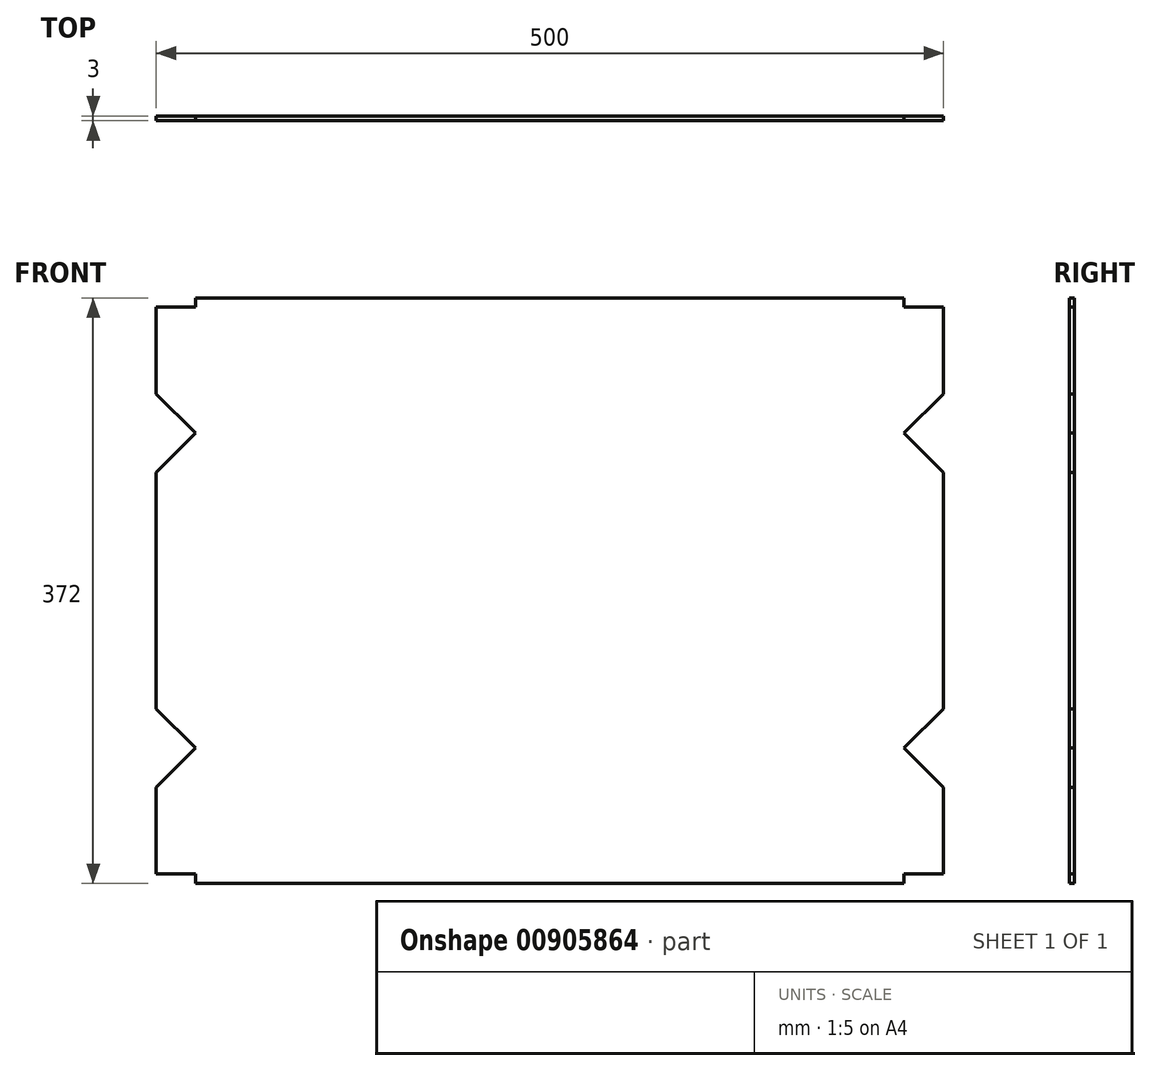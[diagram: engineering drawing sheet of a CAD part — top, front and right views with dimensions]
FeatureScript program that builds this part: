
annotation { "Feature Type Name" : "Feature", "Feature Type Description" : "" }
export const myFeature = defineFeature(function(context is Context, id is Id, definition is map)
    precondition{}
    {
        {
            var Q0;
            Q0=qCreatedBy(makeId("Front.planeOp"),FACE);
            var sketch = newSketch(context, id + "F0", { "sketchPlane" : qUnion([Q0])});
            skLineSegment(sketch, "E0.bottom", {"start": v(225, 186) * mm, "end": v(-225, 186) * mm});
            skLineSegment(sketch, "E0.top", {"start": v(225, -186) * mm, "end": v(-225, -186) * mm});
            skLineSegment(sketch, "E0.left", {"start": v(250, 180) * mm, "end": v(250, 125) * mm});
            skLineSegment(sketch, "E0.right", {"start": v(-250, 180) * mm, "end": v(-250, 125) * mm});
            skPoint(sketch, "E0.middle", {"position": v(0, 0) * mm});
            skLineSegment(sketch, "E1.top", {"start": v(-250, -180) * mm, "end": v(-225, -180) * mm});
            skLineSegment(sketch, "E1.right", {"start": v(-225, -186) * mm, "end": v(-225, -180) * mm});
            skLineSegment(sketch, "E2.top", {"start": v(-250, 180) * mm, "end": v(-225, 180) * mm});
            skLineSegment(sketch, "E2.right", {"start": v(-225, 186) * mm, "end": v(-225, 180) * mm});
            skLineSegment(sketch, "E3.top", {"start": v(250, 180) * mm, "end": v(225, 180) * mm});
            skLineSegment(sketch, "E3.right", {"start": v(225, 186) * mm, "end": v(225, 180) * mm});
            skLineSegment(sketch, "E4.top", {"start": v(250, -180) * mm, "end": v(225, -180) * mm});
            skLineSegment(sketch, "E4.right", {"start": v(225, -186) * mm, "end": v(225, -180) * mm});
            skPoint(sketch, "E5.orphan", {"position": v(-250, -186) * mm});
            skPoint(sketch, "E2.left.start.orphan", {"position": v(-250, 186) * mm});
            skPoint(sketch, "E6.orphan", {"position": v(250, 186) * mm});
            skPoint(sketch, "E7.orphan", {"position": v(250, -186) * mm});
            skLineSegment(sketch, "E8", {"start": v(-250, -180) * mm, "end": v(-250, -125) * mm});
            skLineSegment(sketch, "E9", {"start": v(-225, -100) * mm, "end": v(-250, -125) * mm});
            skLineSegment(sketch, "E10", {"start": v(-250, -75) * mm, "end": v(-225, -100) * mm});
            skLineSegment(sketch, "E11.trimOffspring", {"start": v(-250, -125) * mm, "end": v(-250, -180) * mm});
            skLineSegment(sketch, "E12", {"start": v(-225, -100) * mm, "end": v(-225, 100) * mm});
            skLineSegment(sketch, "E13", {"start": v(-225, 100) * mm, "end": v(-250, 75) * mm});
            skLineSegment(sketch, "E14", {"start": v(-250, 125) * mm, "end": v(-225, 100) * mm});
            skLineSegment(sketch, "E15.trimOffspring", {"start": v(-250, 75) * mm, "end": v(-250, -75) * mm});
            skLineSegment(sketch, "E16", {"start": v(250, -180) * mm, "end": v(250, -125) * mm});
            skLineSegment(sketch, "E17", {"start": v(225, -100) * mm, "end": v(250, -125) * mm});
            skLineSegment(sketch, "E18", {"start": v(250, -75) * mm, "end": v(225, -100) * mm});
            skLineSegment(sketch, "E19.trimOffspring", {"start": v(250, -125) * mm, "end": v(250, -180) * mm});
            skLineSegment(sketch, "E20", {"start": v(225, -100) * mm, "end": v(225, 100) * mm});
            skLineSegment(sketch, "E21", {"start": v(225, 100) * mm, "end": v(250, 75) * mm});
            skLineSegment(sketch, "E22", {"start": v(250, 125) * mm, "end": v(225, 100) * mm});
            skLineSegment(sketch, "E23.trimOffspring", {"start": v(250, 75) * mm, "end": v(250, -75) * mm});
            skSolve(sketch);
        }
        {
            var Q0;
            Q0 = qSketchRegion(id + "F0", true);
            extrude(context, id + "F1", {"entities" : qUnion([Q0]), "depth" : 3 * mm, "offsetDistance" : 25 * mm});
        }
    });
